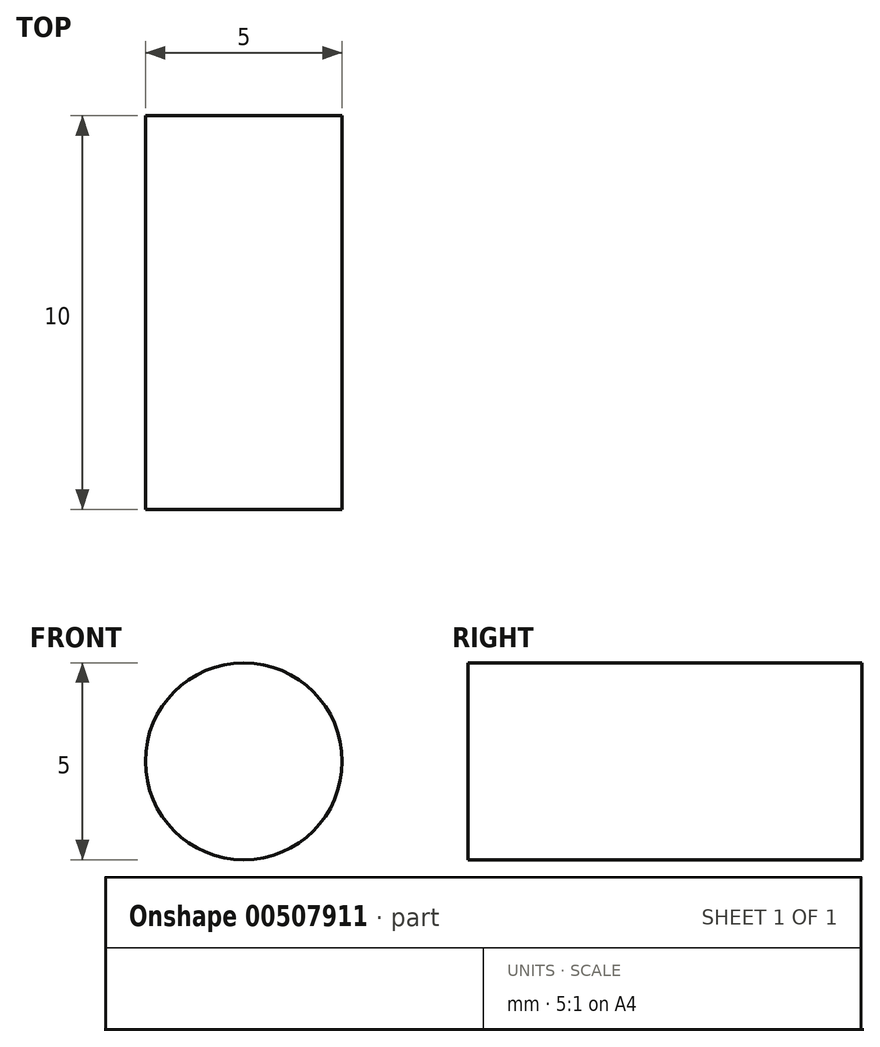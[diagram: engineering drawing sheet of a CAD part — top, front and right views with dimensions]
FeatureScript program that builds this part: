
annotation { "Feature Type Name" : "Feature", "Feature Type Description" : "" }
export const myFeature = defineFeature(function(context is Context, id is Id, definition is map)
    precondition{}
    {
        {
            var Q0;
            Q0=qCreatedBy(makeId("Front.planeOp"),FACE);
            var sketch = newSketch(context, id + "F0", { "sketchPlane" : qUnion([Q0])});
            skCircle(sketch, "E0", {"center": v(0, 0) * mm, "radius": 2.5 * mm});
            skSolve(sketch);
        }
        {
            var Q0;
            Q0=makeQuery(id+"F0.imprint","IMPRINT",FACE,{"disambiguationData":[TD([[makeQuery(id+"F0.imprint","IMPRINT",EDGE,{"derivedFrom":sQuery(id+"F0.wireOp",EDGE,"E0")}),1.0]])]});
            extrude(context, id + "F1", {"entities" : qUnion([Q0]), "depth" : 10 * mm, "offsetDistance" : 25 * mm});
        }
    });
